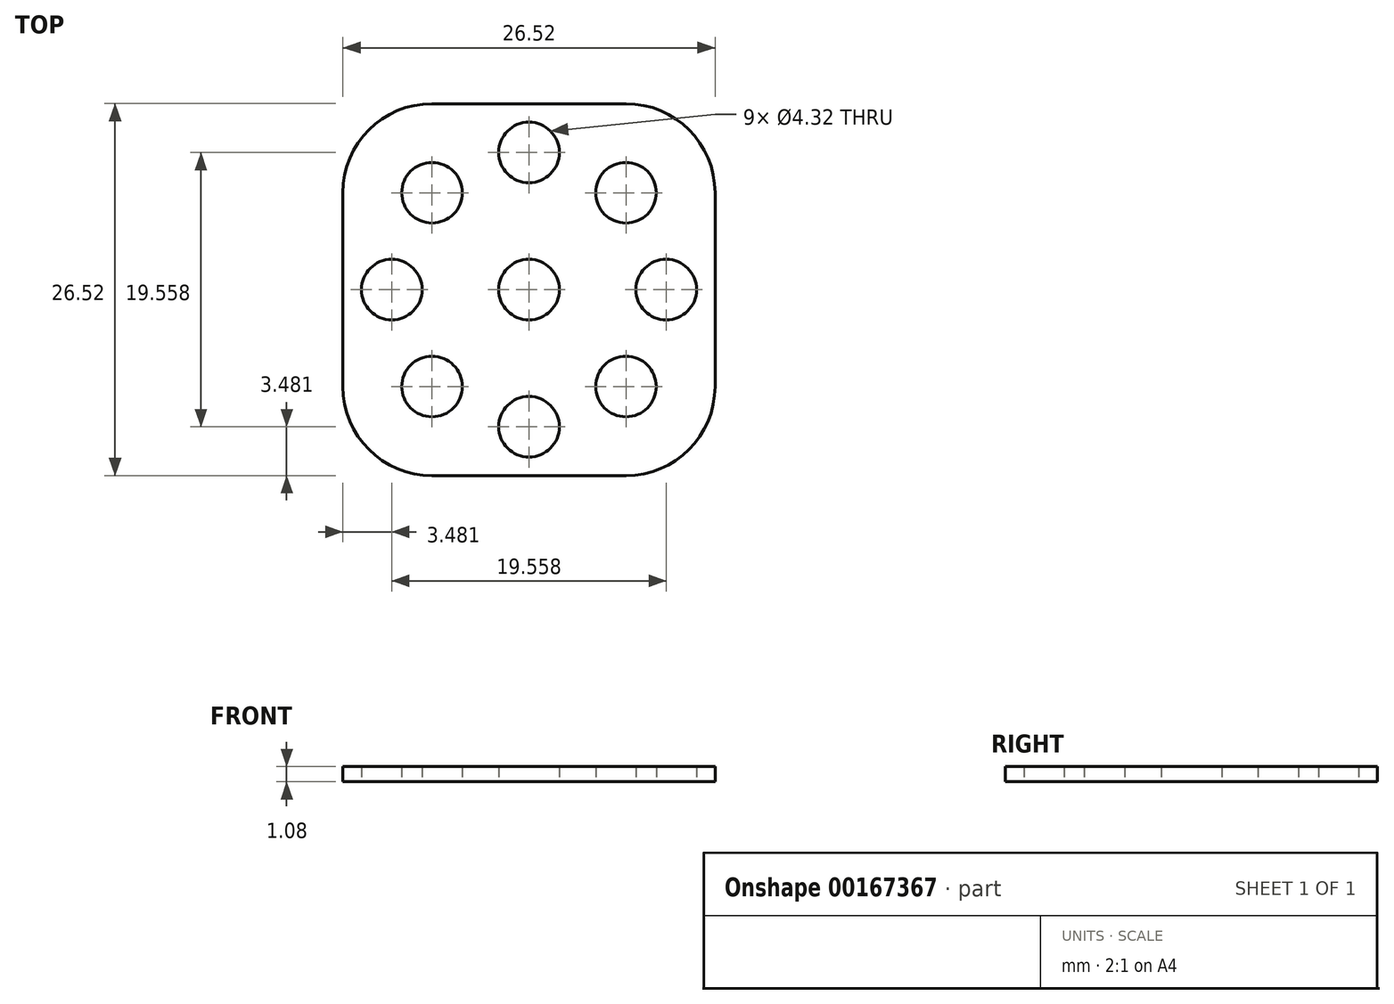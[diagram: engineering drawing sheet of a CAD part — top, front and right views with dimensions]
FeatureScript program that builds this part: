
annotation { "Feature Type Name" : "Feature", "Feature Type Description" : "" }
export const myFeature = defineFeature(function(context is Context, id is Id, definition is map)
    precondition{}
    {
        {
            var Q0;
            Q0=qCreatedBy(makeId("Top.planeOp"),FACE);
            var sketch = newSketch(context, id + "F0", { "sketchPlane" : qUnion([Q0])});
            skLineSegment(sketch, "E0.bottom", {"start": v(6.9, 13.26) * mm, "end": v(-6.9, 13.26) * mm});
            skLineSegment(sketch, "E0.top", {"start": v(6.9, -13.26) * mm, "end": v(-6.9, -13.26) * mm});
            skLineSegment(sketch, "E0.left", {"start": v(13.26, 6.9) * mm, "end": v(13.26, -6.9) * mm});
            skLineSegment(sketch, "E0.right", {"start": v(-13.26, 6.9) * mm, "end": v(-13.26, -6.9) * mm});
            skPoint(sketch, "E0.middle", {"position": v(0, 0) * mm});
            skCircle(sketch, "E1", {"center": v(0, 0) * mm, "radius": 2.16 * mm});
            skCircle(sketch, "E2", {"center": v(-6.9, 6.9) * mm, "radius": 2.16 * mm});
            skCircle(sketch, "E3", {"center": v(-9.78, 0) * mm, "radius": 2.16 * mm});
            skCircle(sketch, "E4", {"center": v(-6.9, -6.9) * mm, "radius": 2.16 * mm});
            skCircle(sketch, "E5", {"center": v(6.9, -6.9) * mm, "radius": 2.16 * mm});
            skCircle(sketch, "E6", {"center": v(9.78, 0) * mm, "radius": 2.16 * mm});
            skCircle(sketch, "E7", {"center": v(6.9, 6.9) * mm, "radius": 2.16 * mm});
            skLineSegment(sketch, "E8", {"start": v(-6.9, 6.9) * mm, "end": v(6.9, 6.9) * mm, "construction": true});
            skLineSegment(sketch, "E9", {"start": v(6.9, -6.9) * mm, "end": v(-6.9, -6.9) * mm, "construction": true});
            skLineSegment(sketch, "E10", {"start": v(-6.9, -6.9) * mm, "end": v(-6.9, 6.9) * mm, "construction": true});
            skLineSegment(sketch, "E11", {"start": v(6.9, 6.9) * mm, "end": v(6.9, -6.9) * mm, "construction": true});
            skLineSegment(sketch, "E12", {"start": v(-6.9, -6.9) * mm, "end": v(6.9, 6.9) * mm, "construction": true});
            skLineSegment(sketch, "E13", {"start": v(0, 13.26) * mm, "end": v(0, -13.26) * mm, "construction": true});
            skCircle(sketch, "E14", {"center": v(0, 9.78) * mm, "radius": 2.16 * mm});
            skCircle(sketch, "E15", {"center": v(0, -9.78) * mm, "radius": 2.16 * mm});
            skPoint(sketch, "E16.visualSharp", {"position": v(-13.26, 13.26) * mm});
            skArc(sketch, "E16.filletArc", {"start": v(-6.9, 13.26) * mm, "mid": v(-11.4, 11.4) * mm, "end": v(-13.26, 6.9) * mm});
            skPoint(sketch, "E17.visualSharp", {"position": v(13.26, 13.26) * mm});
            skArc(sketch, "E17.filletArc", {"start": v(13.26, 6.9) * mm, "mid": v(11.4, 11.4) * mm, "end": v(6.9, 13.26) * mm});
            skPoint(sketch, "E18.visualSharp", {"position": v(13.26, -13.26) * mm});
            skArc(sketch, "E18.filletArc", {"start": v(6.9, -13.26) * mm, "mid": v(11.4, -11.4) * mm, "end": v(13.26, -6.9) * mm});
            skPoint(sketch, "E19.visualSharp", {"position": v(-13.26, -13.26) * mm});
            skArc(sketch, "E19.filletArc", {"start": v(-13.26, -6.9) * mm, "mid": v(-11.4, -11.4) * mm, "end": v(-6.9, -13.26) * mm});
            skLineSegment(sketch, "E20", {"start": v(-13.26, 0) * mm, "end": v(13.26, 0) * mm, "construction": true});
            skSolve(sketch);
        }
        {
            var Q0;
            Q0=qSketchRegion(id+"F0",true);
            extrude(context, id + "F1", {"entities" : qUnion([Q0]), "depth" : 1.08 * mm});
        }
    });
